# Revit family: O4IDB_10BF
name_source: partatom
category: Mechanical Equipment
units: mm (PartAtom-declared; Revit-internal decimal feet)

## family parameters
Always vertical = Yes
Cut with Voids When Loaded = No
OmniClass Number = 23.40.40.11.17
OmniClass Title = Refrigerated Cases
Part Type = Normal
Room Calculation Point = No
Round Connector Dimension = Use Radius
Shared = No
Work Plane-Based = Yes

## types (12) — shared parameters
ANTI SWEAT HEATER AMPS = 1 A
BASE HEIGHT = 10"
BTU PER FOOT CONVENTIONAL = 2189
BTU PER FOOT PARALLEL = 1976
CERTIFICATIONS = NSF 7, UL471, CSA
COIL REFRIGERATION CHARGE = 0.00 lb
CONTROL TYPE = T-STAT
DATE = 05/22/12
DEDICATED CIRCUIT = YES
DEFROST PHASE = 1
DEFROST TIME AND DURATION = 2 @ 60 MIN
DEFROST WATTAGE = 0 W
DIEBOARD HEIGHT = 0"
DISCHARGE AIR TEMPERATURE = 25 °F
DRAIN LINE CONNECTION = Drain Connection
DRAIN LINE DIAMETER = 2"
DRAIN LINE RADIUS = 1"
DRAIN PIPE LENGTH = 0"
DRAIN PIPE TYPE = PVC
DRIP PAN PLUMB TYPE = HARD
Default Elevation = 48"
Description = Wide Multi-Deck Island Merchandiser
ELECTRIC DEFROST = No
ELECTRICAL DEFROST VOLTAGE = 0 V
EQUIPMENT MARK = O4IDB
EVAPORATOR TEMPERATURE = 17 °F
FAN CONNECTOR DESCRIPTION = FAN AND ANTI SWEAT CONNECTOR
FAN NUMBER OF POLES = 1
FAN TYPE = ECM
GROUND FAULT PROTECTION = NO
HEIGHT = 61 11/16"
HOT GAS DEFROST = No
ISOLATED GROUND REQUIRED = NO
Keynote = Deli / Meat
LED LIGHTING AMPS PER ROW = 0 A
LIGHT TYPE = T8 FLUORESCENT
LIGHTING CONNECTION DESCRIPTION = LIGHTING CONNECTOR
LIGHTING NUMBER OF POLES = 1
LIQUID LINE CONNECTION = LIQUID LINE CONNECTION
LIQUID LINE DIAMETER = 0"
LIQUID LINE RADIUS = 0"
Manufacturer = HILL PHOENIX
NUMBER OF WIRES = 3
PHASE = 1
POWER FACTOR = 1
PRESSURE REGULATOR = 0.00 psi
RECEPTICAL MOUNTING HEIGHT ABOVE FLOOR = 19 3/4"
REF PLANE FRONT BACK = 39 7/8"
REVERSE AIR DEFROST = No
SET BACK MODE FOR ENERGY CONSERVATION = NO
SIZE OF COLD WATER HOOK UP = 0"
SIZE OF HOT WATER HOOK-UP = 0"
SUCTION LINE CONNECTION = SUCTION LINE CONNECTION
SUCTION LINE DIAMETER = 1"
SUCTION LINE RADIUS = 0"
T8 LIGHT OR LED LIGHT = Yes
TIME OFF DEFROST = Yes
TOEKICK HEIGHT = 5 1/2"
TOEKICK INSET = 1 1/2"
URL = http://www.hillphoenix.com
VOLTAGE = 120 V
WATER LINE MOUNTING HEIGHT ABOVE FLOOR = 0"
WEIGHT = 0.00 lb
WIDTH = 79 3/4"
zero-valued in all types: CORNICE AND NOSE LIGHT ROWS

## per-type parameters (varying)
- O4IDB-8', TOP SILL SD: ANTI SWEAT APPARENT LOAD=106 VA; ANTI SWEAT HEATER WATTAGE=106 W; BTU ADD FOR LIGHTS=1920; BTU ADD PER SHELF PER FOOT=80; CONVENTIONAL EVAPORATOR LOAD=19432; DEFROST AMPS=8 A; ELECTRICAL JUNCTION HORIZONTAL=26 15/16"; ELECTRICAL JUNCTION VERTICAL=16 11/16"; FAN AMPS=1 A; FAN AND ANTI SWEAT HEATER APPARENT LOAD=190 VA; FAN APPARENT LOAD=84 VA; FAN QUANTITY=6; FAN WATTAGE=42 W; LED LIGHTING AMPS=1 A; LED LIGHTING BTU ADD PER ROW=36; LED LIGHTING WATTAGE=94 W; LEGEND NUMBER=O4IDB-8'; LENGTH=100 3/4"; LENGTH FOR BTU=8; LIGHT AMPS=2 A; LIGHTING APPARENT LOAD=216 VA; LIGHTING WATTAGE=216 VA; Model=O4IDB-8'; PARALLEL EVAPORATOR LOAD=17728; REF PLANE LEFT RIGHT=50 3/8"; SHELF LIGHT ROWS=3; T8 LIGHTING AMPS=2 A; T8 LIGHTING AMPS PER ROW=1 A; T8 LIGHTING BTU ADD PER ROW=80; T8 LIGHTING WATTAGE=216 W; TOTAL APPARENT FAN-LIGHT AND A/S LOAD=364 VA; TOTAL CASE AMPS=3 A; TOTAL CASE WATTAGE=364 W
- O4IDB-12',TOP SILL SD: ANTI SWEAT APPARENT LOAD=149 VA; ANTI SWEAT HEATER WATTAGE=149 W; BTU ADD FOR LIGHTS=4800; BTU ADD PER SHELF PER FOOT=80; CONVENTIONAL EVAPORATOR LOAD=31068; DEFROST AMPS=12 A; ELECTRICAL JUNCTION HORIZONTAL=121 13/16"; ELECTRICAL JUNCTION VERTICAL=56 9/16"; FAN AMPS=1 A; FAN AND ANTI SWEAT HEATER APPARENT LOAD=262 VA; FAN APPARENT LOAD=113 VA; FAN QUANTITY=8; FAN WATTAGE=56 W; LED LIGHTING AMPS=2 A; LED LIGHTING BTU ADD PER ROW=36; LED LIGHTING WATTAGE=270 W; LEGEND NUMBER=O4IDB-12'; LENGTH=148 3/4"; LENGTH FOR BTU=12; LIGHT AMPS=5 A; LIGHTING APPARENT LOAD=618 VA; LIGHTING WATTAGE=618 VA; Model=O4IDB-12'; PARALLEL EVAPORATOR LOAD=28512; REF PLANE LEFT RIGHT=74 3/8"; SHELF LIGHT ROWS=5; T8 LIGHTING AMPS=5 A; T8 LIGHTING AMPS PER ROW=1 A; T8 LIGHTING BTU ADD PER ROW=80; T8 LIGHTING WATTAGE=618 W; TOTAL APPARENT FAN-LIGHT AND A/S LOAD=823 VA; TOTAL CASE AMPS=7 A; TOTAL CASE WATTAGE=823 W
- O4IDB-6', TOP SILL SD: ANTI SWEAT APPARENT LOAD=76 VA; ANTI SWEAT HEATER WATTAGE=76 W; BTU ADD FOR LIGHTS=1080; BTU ADD PER SHELF PER FOOT=60; CONVENTIONAL EVAPORATOR LOAD=14214; DEFROST AMPS=6 A; ELECTRICAL JUNCTION HORIZONTAL=24"; ELECTRICAL JUNCTION VERTICAL=20"; FAN AMPS=0 A; FAN AND ANTI SWEAT HEATER APPARENT LOAD=132 VA; FAN APPARENT LOAD=56 VA; FAN QUANTITY=4; FAN WATTAGE=28 W; LED LIGHTING AMPS=0 A; LED LIGHTING BTU ADD PER ROW=27; LED LIGHTING WATTAGE=58 W; LEGEND NUMBER=O4IDB-6'; LENGTH=76 3/4"; LENGTH FOR BTU=6; LIGHT AMPS=1 A; LIGHTING APPARENT LOAD=144 VA; LIGHTING WATTAGE=144 VA; Model=O4IDB-6'; PARALLEL EVAPORATOR LOAD=12936; REF PLANE LEFT RIGHT=38 3/8"; SHELF LIGHT ROWS=3; T8 LIGHTING AMPS=1 A; T8 LIGHTING AMPS PER ROW=0 A; T8 LIGHTING BTU ADD PER ROW=60; T8 LIGHTING WATTAGE=144 W; TOTAL APPARENT FAN-LIGHT AND A/S LOAD=248 VA; TOTAL CASE AMPS=2 A; TOTAL CASE WATTAGE=248 W
- O4IDB-12',8" SD: ANTI SWEAT APPARENT LOAD=149 VA; ANTI SWEAT HEATER WATTAGE=149 W; BTU ADD FOR LIGHTS=4800; BTU ADD PER SHELF PER FOOT=80; CONVENTIONAL EVAPORATOR LOAD=31068; DEFROST AMPS=12 A; ELECTRICAL JUNCTION HORIZONTAL=121 13/16"; ELECTRICAL JUNCTION VERTICAL=56 9/16"; FAN AMPS=1 A; FAN AND ANTI SWEAT HEATER APPARENT LOAD=262 VA; FAN APPARENT LOAD=113 VA; FAN QUANTITY=8; FAN WATTAGE=56 W; LED LIGHTING AMPS=2 A; LED LIGHTING BTU ADD PER ROW=36; LED LIGHTING WATTAGE=270 W; LEGEND NUMBER=O4IDB-12'; LENGTH=148 3/4"; LENGTH FOR BTU=12; LIGHT AMPS=5 A; LIGHTING APPARENT LOAD=618 VA; LIGHTING WATTAGE=618 VA; Model=O4IDB-12'; PARALLEL EVAPORATOR LOAD=28512; REF PLANE LEFT RIGHT=74 3/8"; SHELF LIGHT ROWS=5; T8 LIGHTING AMPS=5 A; T8 LIGHTING AMPS PER ROW=1 A; T8 LIGHTING BTU ADD PER ROW=80; T8 LIGHTING WATTAGE=618 W; TOTAL APPARENT FAN-LIGHT AND A/S LOAD=823 VA; TOTAL CASE AMPS=7 A; TOTAL CASE WATTAGE=823 W
- O4IDB-6', 8" SD: ANTI SWEAT APPARENT LOAD=76 VA; ANTI SWEAT HEATER WATTAGE=76 W; BTU ADD FOR LIGHTS=1080; BTU ADD PER SHELF PER FOOT=60; CONVENTIONAL EVAPORATOR LOAD=14214; DEFROST AMPS=6 A; ELECTRICAL JUNCTION HORIZONTAL=24"; ELECTRICAL JUNCTION VERTICAL=20"; FAN AMPS=0 A; FAN AND ANTI SWEAT HEATER APPARENT LOAD=132 VA; FAN APPARENT LOAD=56 VA; FAN QUANTITY=4; FAN WATTAGE=28 W; LED LIGHTING AMPS=0 A; LED LIGHTING BTU ADD PER ROW=27; LED LIGHTING WATTAGE=58 W; LEGEND NUMBER=O4IDB-6'; LENGTH=76 3/4"; LENGTH FOR BTU=6; LIGHT AMPS=1 A; LIGHTING APPARENT LOAD=144 VA; LIGHTING WATTAGE=144 VA; Model=O4IDB-6'; PARALLEL EVAPORATOR LOAD=12936; REF PLANE LEFT RIGHT=38 3/8"; SHELF LIGHT ROWS=3; T8 LIGHTING AMPS=1 A; T8 LIGHTING AMPS PER ROW=0 A; T8 LIGHTING BTU ADD PER ROW=60; T8 LIGHTING WATTAGE=144 W; TOTAL APPARENT FAN-LIGHT AND A/S LOAD=248 VA; TOTAL CASE AMPS=2 A; TOTAL CASE WATTAGE=248 W
- O4IDB-8', 8" SD: ANTI SWEAT APPARENT LOAD=106 VA; ANTI SWEAT HEATER WATTAGE=106 W; BTU ADD FOR LIGHTS=1920; BTU ADD PER SHELF PER FOOT=80; CONVENTIONAL EVAPORATOR LOAD=19432; DEFROST AMPS=8 A; ELECTRICAL JUNCTION HORIZONTAL=26 15/16"; ELECTRICAL JUNCTION VERTICAL=16 11/16"; FAN AMPS=1 A; FAN AND ANTI SWEAT HEATER APPARENT LOAD=190 VA; FAN APPARENT LOAD=84 VA; FAN QUANTITY=6; FAN WATTAGE=42 W; LED LIGHTING AMPS=1 A; LED LIGHTING BTU ADD PER ROW=36; LED LIGHTING WATTAGE=94 W; LEGEND NUMBER=O4IDB-8'; LENGTH=100 3/4"; LENGTH FOR BTU=8; LIGHT AMPS=2 A; LIGHTING APPARENT LOAD=216 VA; LIGHTING WATTAGE=216 VA; Model=O4IDB-8'; PARALLEL EVAPORATOR LOAD=17728; REF PLANE LEFT RIGHT=50 3/8"; SHELF LIGHT ROWS=3; T8 LIGHTING AMPS=2 A; T8 LIGHTING AMPS PER ROW=1 A; T8 LIGHTING BTU ADD PER ROW=80; T8 LIGHTING WATTAGE=216 W; TOTAL APPARENT FAN-LIGHT AND A/S LOAD=364 VA; TOTAL CASE AMPS=3 A; TOTAL CASE WATTAGE=364 W
- O4IDB-12',10", 12", 14", 16" SD: ANTI SWEAT APPARENT LOAD=149 VA; ANTI SWEAT HEATER WATTAGE=149 W; BTU ADD FOR LIGHTS=4800; BTU ADD PER SHELF PER FOOT=80; CONVENTIONAL EVAPORATOR LOAD=31068; DEFROST AMPS=12 A; ELECTRICAL JUNCTION HORIZONTAL=121 13/16"; ELECTRICAL JUNCTION VERTICAL=56 9/16"; FAN AMPS=1 A; FAN AND ANTI SWEAT HEATER APPARENT LOAD=262 VA; FAN APPARENT LOAD=113 VA; FAN QUANTITY=8; FAN WATTAGE=56 W; LED LIGHTING AMPS=2 A; LED LIGHTING BTU ADD PER ROW=36; LED LIGHTING WATTAGE=270 W; LEGEND NUMBER=O4IDB-12'; LENGTH=148 3/4"; LENGTH FOR BTU=12; LIGHT AMPS=5 A; LIGHTING APPARENT LOAD=618 VA; LIGHTING WATTAGE=618 VA; Model=O4IDB-12'; PARALLEL EVAPORATOR LOAD=28512; REF PLANE LEFT RIGHT=74 3/8"; SHELF LIGHT ROWS=5; T8 LIGHTING AMPS=5 A; T8 LIGHTING AMPS PER ROW=1 A; T8 LIGHTING BTU ADD PER ROW=80; T8 LIGHTING WATTAGE=618 W; TOTAL APPARENT FAN-LIGHT AND A/S LOAD=823 VA; TOTAL CASE AMPS=7 A; TOTAL CASE WATTAGE=823 W
- O4IDB-6',10", 12", 14", 16" SD: ANTI SWEAT APPARENT LOAD=76 VA; ANTI SWEAT HEATER WATTAGE=76 W; BTU ADD FOR LIGHTS=1080; BTU ADD PER SHELF PER FOOT=60; CONVENTIONAL EVAPORATOR LOAD=14214; DEFROST AMPS=6 A; ELECTRICAL JUNCTION HORIZONTAL=24"; ELECTRICAL JUNCTION VERTICAL=20"; FAN AMPS=0 A; FAN AND ANTI SWEAT HEATER APPARENT LOAD=132 VA; FAN APPARENT LOAD=56 VA; FAN QUANTITY=4; FAN WATTAGE=28 W; LED LIGHTING AMPS=0 A; LED LIGHTING BTU ADD PER ROW=27; LED LIGHTING WATTAGE=58 W; LEGEND NUMBER=O4IDB-6'; LENGTH=76 3/4"; LENGTH FOR BTU=6; LIGHT AMPS=1 A; LIGHTING APPARENT LOAD=144 VA; LIGHTING WATTAGE=144 VA; Model=O4IDB-6'; PARALLEL EVAPORATOR LOAD=12936; REF PLANE LEFT RIGHT=38 3/8"; SHELF LIGHT ROWS=3; T8 LIGHTING AMPS=1 A; T8 LIGHTING AMPS PER ROW=0 A; T8 LIGHTING BTU ADD PER ROW=60; T8 LIGHTING WATTAGE=144 W; TOTAL APPARENT FAN-LIGHT AND A/S LOAD=248 VA; TOTAL CASE AMPS=2 A; TOTAL CASE WATTAGE=248 W
- O4IDB-8',10", 12", 14", 16" SD: ANTI SWEAT APPARENT LOAD=106 VA; ANTI SWEAT HEATER WATTAGE=106 W; BTU ADD FOR LIGHTS=1920; BTU ADD PER SHELF PER FOOT=80; CONVENTIONAL EVAPORATOR LOAD=19432; DEFROST AMPS=8 A; ELECTRICAL JUNCTION HORIZONTAL=26 15/16"; ELECTRICAL JUNCTION VERTICAL=16 11/16"; FAN AMPS=1 A; FAN AND ANTI SWEAT HEATER APPARENT LOAD=190 VA; FAN APPARENT LOAD=84 VA; FAN QUANTITY=6; FAN WATTAGE=42 W; LED LIGHTING AMPS=1 A; LED LIGHTING BTU ADD PER ROW=36; LED LIGHTING WATTAGE=94 W; LEGEND NUMBER=O4IDB-8'; LENGTH=100 3/4"; LENGTH FOR BTU=8; LIGHT AMPS=2 A; LIGHTING APPARENT LOAD=216 VA; LIGHTING WATTAGE=216 VA; Model=O4IDB-8'; PARALLEL EVAPORATOR LOAD=17728; REF PLANE LEFT RIGHT=50 3/8"; SHELF LIGHT ROWS=3; T8 LIGHTING AMPS=2 A; T8 LIGHTING AMPS PER ROW=1 A; T8 LIGHTING BTU ADD PER ROW=80; T8 LIGHTING WATTAGE=216 W; TOTAL APPARENT FAN-LIGHT AND A/S LOAD=364 VA; TOTAL CASE AMPS=3 A; TOTAL CASE WATTAGE=364 W
- O4IDB-6': ANTI SWEAT APPARENT LOAD=76 VA; ANTI SWEAT HEATER WATTAGE=76 W; BTU ADD FOR LIGHTS=1080; BTU ADD PER SHELF PER FOOT=60; CONVENTIONAL EVAPORATOR LOAD=14214; DEFROST AMPS=6 A; ELECTRICAL JUNCTION HORIZONTAL=24"; ELECTRICAL JUNCTION VERTICAL=20"; FAN AMPS=0 A; FAN AND ANTI SWEAT HEATER APPARENT LOAD=132 VA; FAN APPARENT LOAD=56 VA; FAN QUANTITY=4; FAN WATTAGE=28 W; LED LIGHTING AMPS=0 A; LED LIGHTING BTU ADD PER ROW=27; LED LIGHTING WATTAGE=58 W; LEGEND NUMBER=O4IDB-6'; LENGTH=76 3/4"; LENGTH FOR BTU=6; LIGHT AMPS=1 A; LIGHTING APPARENT LOAD=144 VA; LIGHTING WATTAGE=144 VA; Model=O4IDB-6'; PARALLEL EVAPORATOR LOAD=12936; REF PLANE LEFT RIGHT=38 3/8"; SHELF LIGHT ROWS=3; T8 LIGHTING AMPS=1 A; T8 LIGHTING AMPS PER ROW=0 A; T8 LIGHTING BTU ADD PER ROW=60; T8 LIGHTING WATTAGE=144 W; TOTAL APPARENT FAN-LIGHT AND A/S LOAD=248 VA; TOTAL CASE AMPS=2 A; TOTAL CASE WATTAGE=248 W
- O4IDB-12': ANTI SWEAT APPARENT LOAD=149 VA; ANTI SWEAT HEATER WATTAGE=149 W; BTU ADD FOR LIGHTS=4800; BTU ADD PER SHELF PER FOOT=80; CONVENTIONAL EVAPORATOR LOAD=31068; DEFROST AMPS=12 A; ELECTRICAL JUNCTION HORIZONTAL=121 13/16"; ELECTRICAL JUNCTION VERTICAL=56 9/16"; FAN AMPS=1 A; FAN AND ANTI SWEAT HEATER APPARENT LOAD=262 VA; FAN APPARENT LOAD=113 VA; FAN QUANTITY=8; FAN WATTAGE=56 W; LED LIGHTING AMPS=2 A; LED LIGHTING BTU ADD PER ROW=36; LED LIGHTING WATTAGE=270 W; LEGEND NUMBER=O4IDB-12'; LENGTH=148 3/4"; LENGTH FOR BTU=12; LIGHT AMPS=5 A; LIGHTING APPARENT LOAD=618 VA; LIGHTING WATTAGE=618 VA; Model=O4IDB-12'; PARALLEL EVAPORATOR LOAD=28512; REF PLANE LEFT RIGHT=74 3/8"; SHELF LIGHT ROWS=5; T8 LIGHTING AMPS=5 A; T8 LIGHTING AMPS PER ROW=1 A; T8 LIGHTING BTU ADD PER ROW=80; T8 LIGHTING WATTAGE=618 W; TOTAL APPARENT FAN-LIGHT AND A/S LOAD=823 VA; TOTAL CASE AMPS=7 A; TOTAL CASE WATTAGE=823 W
- O4IDB-8': ANTI SWEAT APPARENT LOAD=106 VA; ANTI SWEAT HEATER WATTAGE=106 W; BTU ADD FOR LIGHTS=1920; BTU ADD PER SHELF PER FOOT=80; CONVENTIONAL EVAPORATOR LOAD=19432; DEFROST AMPS=8 A; ELECTRICAL JUNCTION HORIZONTAL=26 15/16"; ELECTRICAL JUNCTION VERTICAL=16 11/16"; FAN AMPS=1 A; FAN AND ANTI SWEAT HEATER APPARENT LOAD=190 VA; FAN APPARENT LOAD=84 VA; FAN QUANTITY=6; FAN WATTAGE=42 W; LED LIGHTING AMPS=1 A; LED LIGHTING BTU ADD PER ROW=36; LED LIGHTING WATTAGE=94 W; LEGEND NUMBER=O4IDB-8'; LENGTH=100 3/4"; LENGTH FOR BTU=8; LIGHT AMPS=2 A; LIGHTING APPARENT LOAD=216 VA; LIGHTING WATTAGE=216 VA; Model=O4IDB-8'; PARALLEL EVAPORATOR LOAD=17728; REF PLANE LEFT RIGHT=50 3/8"; SHELF LIGHT ROWS=3; T8 LIGHTING AMPS=2 A; T8 LIGHTING AMPS PER ROW=1 A; T8 LIGHTING BTU ADD PER ROW=80; T8 LIGHTING WATTAGE=216 W; TOTAL APPARENT FAN-LIGHT AND A/S LOAD=364 VA; TOTAL CASE AMPS=3 A; TOTAL CASE WATTAGE=364 W

## geometry (parser evidence)
native form markers: Blend x2, Sweep x6
no freeform markers — native parametric forms only
